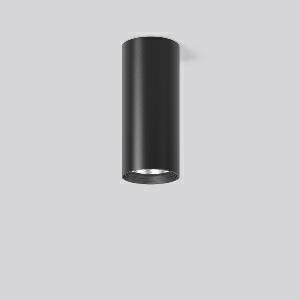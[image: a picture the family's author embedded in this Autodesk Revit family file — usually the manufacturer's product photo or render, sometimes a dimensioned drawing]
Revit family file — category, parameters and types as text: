
# Revit family: heledon_mini_a_931208_003_3_76_3ef8
name_source: partatom
category: Lighting Fixtures
units: mm (PartAtom-declared; Revit-internal decimal feet)

## family parameters
Cut with Voids When Loaded = No
Host = Face
Light Source = No
Part Type = Normal
Room Calculation Point = No
Round Connector Dimension = Use Diameter
Shared = No

## types (1)
- HELEDON mini A (1 x LED Modul 935, 3700 lm, 3500)
    Apparent Load = 29 VA
    Approval mark = CE
    CIE Flux Codes = 100 100 100 100 100
    Color Rendering = 92
    Color Temperature = 3500
    Default Elevation = 1800 mm
    Description = Series: HELEDON mini
Cylindrical surface-mounted downlight. Housing: die-cast aluminium, powder-coated. Internal ceiling frame polycarbonate with bayonet mounting. Black plastic ring and recessed LED to prevent glare from the side. Optical assembly with reflector made of MIRO-Silver with 98% total light reflection for outstanding efficiency - can be changed without tools. Best colour rendering index Ra>90. Suitable for Ceiling mounting. Easy installation with a separate ceiling frame with bayonet mounting and plug connection. Driver integrated. Connected via plug-in connector. High quality converter without flickering and stroboscopic effect. The following accessories can be mounted without use of tools: interchangeable lenses, decorative glasses, honeycomb louvre, clear and frosted diffusers, white interchangeable plastic ring. 
Colour: deep black, matt (RAL 9005)
Diameter: 87 mm
Height: 197 mm
Lamp: LED
Socket: without socket
Colour temperature: 3500K
Colour rendering index (CRI): 92
System power: 29 W
Rated luminous flux: 3700 lm
Luminous efficiency: 128 lm/W
Control gear: Converter, dimmable, DALI
Protection class: I
Type of protection: IP 20
    Height = 197 mm
    Lamp = 1 x LED Modul 935
    Lamp Light Flux = 3700 lm
    Lamp count = 1
    Length = 87 mm
    Lifetime = 50000 h
    Luminous efficacy = 128 lm/W
    Manufacturer = RZB
    ModVariant = No
    Model = 931208.003.3.76
    Mounting Place = Ceiling
    Mounting Type = Surface mounted
    Number of Poles = 1
    OnlyDefault = Yes
    Power Factor = 1
    Product Name = HELEDON mini A
    Product group = Surface mounted downlights
    ProductGroupID = 302
    Protection Class = Protection class I
    Protection Degree = IP 20
    RLX_Detail_Level = 1
    RLX_Emergency_Light_Flux = 0 lm
    RLX_Emergency_Type = 0
    RLX_Emergency_Type_DB = No
    RlxData = <blob elided: 106069 chars, md5=b3d91757>
    Socket = socket
    Standby Power = 0 W
    System Light Flux = 3700 lm
    System Power = 29 W
    Type Comments = Product without accessories
    Type Image = 931188.003.jpg
    URL = http://relux.com
    VarID = ---
    Voltage = 230 V
    Voltage Range = 220-240 V
    Weight = 0.00 kg
    Width = 0 mm  [stored 0 ft]

note: [stored X ft] marks values corroborated as IEEE doubles in the binary element streams (Revit-internal decimal feet)

## geometry (parser evidence)
native form markers: Blend x4, Sweep x9
no freeform markers — native parametric forms only
